# Revit family: LAMP_FIL 70 OPAL D-I
name_source: partatom
category: Luminarias
revit_build: Autodesk Revit 2015 (Build: 20140606_1530(x64)
units: mm (PartAtom-declared; Revit-internal decimal feet)

## types (8) — shared parameters
CRI = 80
Cambio de temperatura de color de luz atenuada = <Ninguno>
Comentarios de tipo = Availability of switching between accessories through visibility parameters when placed in a project.
Fabricante = LAMP
Filtro de color = 16777215
Gear = Electronic
IEE = A++
IFC Clasificación = Light Fixture
Installation instructions = https://www.lamp.es
Insulation class = I
LED Lifetime = 50000 L80 B10
Last update = 11/08/2020
Luminaire type = Indoor - Modular Systems
Lámpara = LED MID-POWER
MacAdam = 3
Manufacturer URL = http://www.lamp.es
Manufacturer country = Spain
Manufacturer name = LAMP
Material Perfil = LAMP_Aluminio Perfil Fil GR
Material difusor = LAMP_PC Difusor Opal Fil
Model explanation = Availability of switching between accessories through visibility parameters when placed in a project.
Power Supply = 220-240V 50-60Hz
Product URL = https://www.lamp.es
Product datasheet = https://www.lamp.es
Protection rating = IP42, IK05
Type = MID POWER PHILIPS
Ángulo de inclinación = 90,00°

## per-type parameters (varying)
| type | Archivo de red fotométrica | Descripción | Dimensions | Efficacy | Finish | Indirect light | Largo | Longitud de línea de emisión | Material codo | Material perfil | Modelo | Plum | Power | Product code | UniClass 1.4 Code | UniClass 2.0 Code | Weight |
| 1162MM 3900LM 3000K GREY | 4741670_dir-WW_100.IES | FIL 70 OPAL D/I SUS 3900 WW GR. | 1162 x 70 x 70 mm | 104 lm/W | Gloss Grey | LAMP_FIL + LED OPAL D-I INDIRECT FOT : IND_1162MM 3900LM 3000K GREY | 1162 mm  [stored 3.81234 ft] | 1162 mm  [stored 3.81234 ft] | LAMP_Aluminio Perfil Fil GR | LAMP_Aluminio Perfil Fil GR | F71SU120MOIO830NG | 30 W | 27 W | F71SU120MOIO830NG | F71SU120MOIO830NG | F71SU120MOIO830NG | 2,85 kg |
| 1162MM 3900LM 3000K WHITE | 4741670_dir-WW_100.IES | FIL 70 OPAL D/I SUS 3900 WW WH. | 1162 x 70 x 70 mm | 104 lm/W | Matt Grey | LAMP_FIL + LED OPAL D-I INDIRECT FOT : IND_1162MM 3900LM 3000K WHITE | 1162 mm  [stored 3.81234 ft] | 1162 mm  [stored 3.81234 ft] | LAMP_Aluminio Perfil Fil BL | LAMP_Aluminio Perfil Fil BL | F71SU120MOIO830NW | 30 W | 27 W | F71SU120MOIO830NW | F71SU120MOIO830NW | F71SU120MOIO830NW | 2,85 kg |
| 1162MM 3900LM 4000K GREY | 4740670_dir-NW_100.IES | FIL 70 OPAL D/I SUS 3900 NW GR. | 1162 x 70 x 70 mm | 111 lm/W | Gloss Grey | LAMP_FIL + LED OPAL D-I INDIRECT FOT : IND_1162MM 3900LM 4000K GREY | 1162 mm  [stored 3.81234 ft] | 1162 mm  [stored 3.81234 ft] | LAMP_Aluminio Perfil Fil GR | LAMP_Aluminio Perfil Fil GR | F71SU120MOIO840NG | 30 W | 27 W | F71SU120MOIO840NG | F71SU120MOIO840NG | F71SU120MOIO840NG | 2,85 kg |
| 1162MM 3900LM 4000K WHITE | 4740670_dir-NW_100.IES | FIL 70 OPAL D/I SUS 3900 NW WH. | 1162 x 70 x 70 mm | 111 lm/W | Matt White | LAMP_FIL + LED OPAL D-I INDIRECT FOT : IND_1162MM 3900LM 4000K WHITE | 1162 mm  [stored 3.81234 ft] | 1162 mm  [stored 3.81234 ft] | LAMP_Aluminio Perfil Fil BL | LAMP_Aluminio Perfil Fil BL | F71SU120MOIO840NW | 30 W | 27 W | F71SU120MOIO840NW | F71SU120MOIO840NW | F71SU120MOIO840NW | 2,85 kg |
| 1743MM 5850LM 3000K GREY | 4741680_dir-WW_100.IES | FIL 70 OPAL D/I SUS 5850 WW GR.
FIL + LED OPAL D/I SUS 5850 WW GR.
FIL + LED OPAL D/I SUS 5850 WW GR. | 1743 x 70 x 70 mm | 112 lm/W | Gloss Grey | LAMP_FIL + LED OPAL D-I INDIRECT FOT : IND_1743MM 5850LM 3000K GREY | 1743 mm  [stored 5.7185 ft] | 1743 mm  [stored 5.7185 ft] | LAMP_Aluminio Perfil Fil GR | LAMP_Aluminio Perfil Fil GR | F71SU170MOIO830NG | 42 W | 37 W | F71SU170MOIO830NG | F71SU170MOIO830NG | F71SU170MOIO830NG | 4,26 kg |
| 1743MM 5850LM 3000K WHITE | 4741680_dir-WW_100.IES | FIL 70 OPAL D/I SUS 5850 WW WH.
FIL + LED OPAL D/I SUS 5850 WW GR.
FIL + LED OPAL D/I SUS 5850 WW GR. | 1743 x 70 x 70 mm | 112 lm/W | Matt White | LAMP_FIL + LED OPAL D-I INDIRECT FOT : IND_1743MM 5850LM 3000K WHITE | 1743 mm  [stored 5.7185 ft] | 1743 mm  [stored 5.7185 ft] | LAMP_Aluminio Perfil Fil BL | LAMP_Aluminio Perfil Fil BL | F71SU170MOIO830NW | 42 W | 37 W | F71SU170MOIO830NW | F71SU170MOIO830NW | F71SU170MOIO830NW | 4,26 kg |
| 1743MM 5850LM 4000K GREY | 4740680_dir-NW_100.IES | FIL 70 OPAL D/I SUS 5850 NW GR.
FIL + LED OPAL D/I SUS 5850 WW GR.
FIL + LED OPAL D/I SUS 5850 WW GR. | 1743 x 70 x 70 mm | 120 lm/W | Gloss Grey | LAMP_FIL + LED OPAL D-I INDIRECT FOT : IND_1743MM 5850LM 4000K GREY | 1743 mm  [stored 5.7185 ft] | 1743 mm  [stored 5.7185 ft] | LAMP_Aluminio Perfil Fil GR | LAMP_Aluminio Perfil Fil GR | F71SU170MOIO840NG | 42 W | 37 W | F71SU170MOIO840NG | F71SU170MOIO840NG | F71SU170MOIO840NG | 4,26 kg |
| 1743MM 5850LM 4000K WHITE | 4740680_dir-NW_100.IES | FIL 70 OPAL D/I SUS 5850 NW WH. | 1743 x 70 x 70 mm | 120 lm/W | Matt White | LAMP_FIL + LED OPAL D-I INDIRECT FOT : IND_1743MM 5850LM 4000K WHITE | 1743 mm  [stored 5.7185 ft] | 1743 mm  [stored 5.7185 ft] | LAMP_Aluminio Perfil Fil BL | LAMP_Aluminio Perfil Fil BL | F71SU170MOIO840NW | 42 W | 37 W | F71SU170MOIO840NW | F71SU170MOIO840NW | F71SU170MOIO840NW | 4,26 kg |

note: [stored X ft] marks values corroborated as IEEE doubles in the binary element streams (Revit-internal decimal feet)

## geometry (parser evidence)
native form markers: Blend x2
no freeform markers — native parametric forms only
